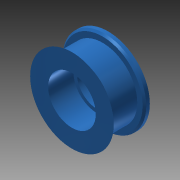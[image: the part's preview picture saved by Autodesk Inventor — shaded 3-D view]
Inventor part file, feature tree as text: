
AUTODESK INVENTOR PART (.ipt)
format: ipt  version: 2013 (Build 170138000, 138)  size: 116,736 bytes
history: native  units: mm
features: revolve x1, sketch x1
ambient origin geometry x8: Origin, YZ Plane, XZ Plane, XY Plane, X Axis, Y Axis, Z Axis, Center Point
bodies: Solid1 (feature_tree)
feature tree (2):
  revolve  "Revolution1"  [1 undecoded]
  sketch  "Sketch1"  dims[d6=10.0mm d7=6.6mm d10=90.0deg d14=5.0mm d17=7.0mm d18=1.5mm d19=135.0deg d20=2.0mm d21=1.0mm d22=3.0mm]
note: 1 required parameter value undecoded (feature->parameter linkage not recoverable at this tier; creation-order binding heuristic only, values carry confidence <= 0.55)
